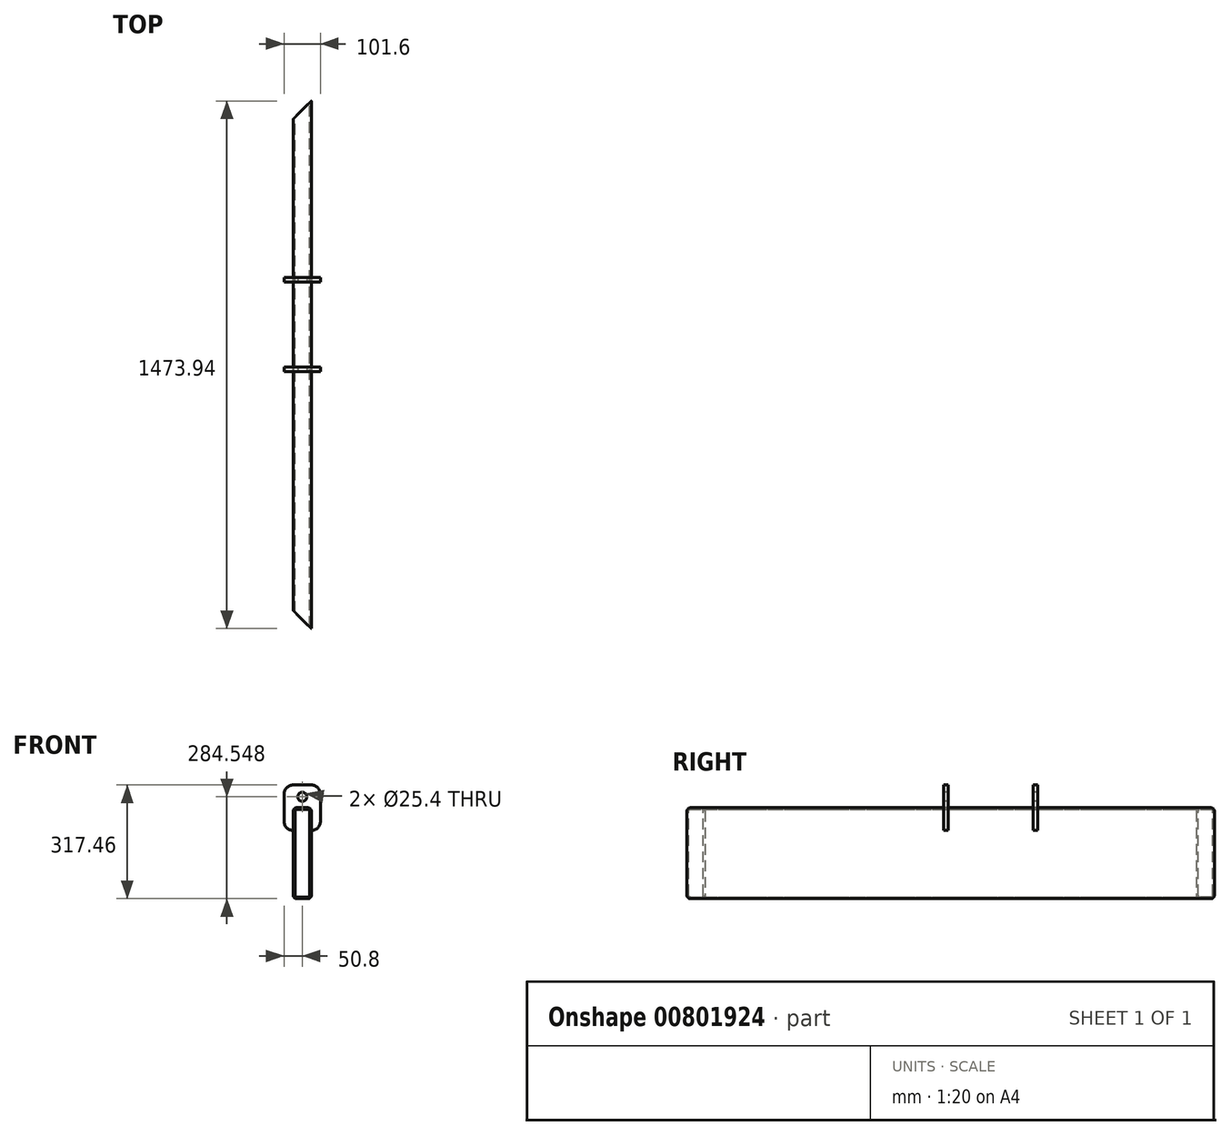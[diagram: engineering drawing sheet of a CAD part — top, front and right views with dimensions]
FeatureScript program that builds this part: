
annotation { "Feature Type Name" : "Feature", "Feature Type Description" : "" }
export const myFeature = defineFeature(function(context is Context, id is Id, definition is map)
    precondition{}
    {
        {
            var Q0;
            Q0=qCreatedBy(makeId("Front.planeOp"),FACE);
            var sketch = newSketch(context, id + "F0", { "sketchPlane" : qUnion([Q0])});
            skLineSegment(sketch, "E0.bottom", {"start": v(-9.52, 0) * mm, "end": v(-41.28, 0) * mm});
            skLineSegment(sketch, "E0.top", {"start": v(-9.53, 254) * mm, "end": v(-41.28, 254) * mm});
            skLineSegment(sketch, "E0.left", {"start": v(0, 9.53) * mm, "end": v(0, 244.47) * mm});
            skLineSegment(sketch, "E0.right", {"start": v(-50.8, 9.52) * mm, "end": v(-50.8, 244.47) * mm});
            skLineSegment(sketch, "E1.bottom", {"start": v(-41.3, 249.25) * mm, "end": v(-9.5, 249.25) * mm});
            skLineSegment(sketch, "E1.top", {"start": v(-41.3, 4.75) * mm, "end": v(-9.5, 4.75) * mm});
            skLineSegment(sketch, "E1.left", {"start": v(-46.05, 244.5) * mm, "end": v(-46.05, 9.5) * mm});
            skLineSegment(sketch, "E1.right", {"start": v(-4.75, 244.5) * mm, "end": v(-4.75, 9.5) * mm});
            skPoint(sketch, "E2.visualSharp", {"position": v(-46.05, 249.25) * mm});
            skArc(sketch, "E2.filletArc", {"start": v(-41.3, 249.25) * mm, "mid": v(-44.66, 247.86) * mm, "end": v(-46.05, 244.5) * mm});
            skPoint(sketch, "E3.visualSharp", {"position": v(-4.75, 249.25) * mm});
            skArc(sketch, "E3.filletArc", {"start": v(-4.75, 244.5) * mm, "mid": v(-6.14, 247.86) * mm, "end": v(-9.5, 249.25) * mm});
            skPoint(sketch, "E4.visualSharp", {"position": v(-4.75, 4.75) * mm});
            skArc(sketch, "E4.filletArc", {"start": v(-9.5, 4.75) * mm, "mid": v(-6.14, 6.14) * mm, "end": v(-4.75, 9.5) * mm});
            skPoint(sketch, "E5.visualSharp", {"position": v(-46.05, 4.75) * mm});
            skArc(sketch, "E5.filletArc", {"start": v(-46.05, 9.5) * mm, "mid": v(-44.66, 6.14) * mm, "end": v(-41.3, 4.75) * mm});
            skPoint(sketch, "E6.visualSharp", {"position": v(-50.8, 254) * mm});
            skArc(sketch, "E6.filletArc", {"start": v(-41.28, 254) * mm, "mid": v(-48.01, 251.21) * mm, "end": v(-50.8, 244.47) * mm});
            skPoint(sketch, "E7.visualSharp", {"position": v(0, 254) * mm});
            skArc(sketch, "E7.filletArc", {"start": v(0, 244.47) * mm, "mid": v(-2.79, 251.21) * mm, "end": v(-9.53, 254) * mm});
            skPoint(sketch, "E8.visualSharp", {"position": v(0, 0) * mm});
            skArc(sketch, "E8.filletArc", {"start": v(-9.52, 0) * mm, "mid": v(-2.79, 2.79) * mm, "end": v(0, 9.53) * mm});
            skPoint(sketch, "E9.visualSharp", {"position": v(-50.8, 0) * mm});
            skArc(sketch, "E9.filletArc", {"start": v(-50.8, 9.52) * mm, "mid": v(-48.01, 2.79) * mm, "end": v(-41.28, 0) * mm});
            skSolve(sketch);
        }
        {
            var Q0;
            Q0=qSketchRegion(id+"F0",true);
            extrude(context, id + "F1", {"entities" : qUnion([Q0]), "depth" : 1473.94 * mm});
        }
        {
            var Q0;
            Q0=makeQuery(id+"F1.opExtrude","SWEPT_FACE",FACE,{"disambiguationData":[OSD([sQuery(id+"F0.wireOp",EDGE,"E0.top")])]});
            var sketch = newSketch(context, id + "F2", { "sketchPlane" : qUnion([Q0])});
            skLineSegment(sketch, "E10", {"start": v(-50.8, -1473.94) * mm, "end": v(0, -1423.14) * mm});
            skLineSegment(sketch, "E11", {"start": v(0, -1423.14) * mm, "end": v(0, -1473.94) * mm});
            skLineSegment(sketch, "E12", {"start": v(0, -1473.94) * mm, "end": v(-50.8, -1473.94) * mm});
            skLineSegment(sketch, "E13", {"start": v(-50.8, 0) * mm, "end": v(0, -50.8) * mm});
            skLineSegment(sketch, "E14", {"start": v(0, -50.8) * mm, "end": v(0, 0) * mm});
            skLineSegment(sketch, "E15", {"start": v(0, 0) * mm, "end": v(-50.8, 0) * mm});
            skSolve(sketch);
        }
        {
            var Q0;
            Q0=qSketchRegion(id+"F2",true);
            extrude(context, id + "F3", {"entities" : qUnion([Q0]), "operationType" : NewBodyOperationType.REMOVE, "endBound" : BoundingType.THROUGH_ALL, "oppositeDirection" : true, "depth" : 25.4 * mm});
        }
        {
            var Q0;
            Q0=makeQuery(id+"F1.opExtrude","SWEPT_BODY",BODY,{"disambiguationData":[OSD([sQuery(id+"F0.wireOp",EDGE,"E0.bottom"),sQuery(id+"F0.wireOp",EDGE,"E0.top"),sQuery(id+"F0.wireOp",EDGE,"E0.left"),sQuery(id+"F0.wireOp",EDGE,"E0.right"),sQuery(id+"F0.wireOp",EDGE,"E1.bottom"),sQuery(id+"F0.wireOp",EDGE,"E1.top"),sQuery(id+"F0.wireOp",EDGE,"E1.left"),sQuery(id+"F0.wireOp",EDGE,"E1.right"),sQuery(id+"F0.wireOp",EDGE,"E2.filletArc"),sQuery(id+"F0.wireOp",EDGE,"E3.filletArc"),sQuery(id+"F0.wireOp",EDGE,"E4.filletArc"),sQuery(id+"F0.wireOp",EDGE,"E5.filletArc"),sQuery(id+"F0.wireOp",EDGE,"E6.filletArc"),sQuery(id+"F0.wireOp",EDGE,"E7.filletArc"),sQuery(id+"F0.wireOp",EDGE,"E8.filletArc"),sQuery(id+"F0.wireOp",EDGE,"E9.filletArc")])]});
            var Q1;
            Q1=makeQuery(id+"F1.opExtrude","SWEPT_EDGE",EDGE,{"disambiguationData":[OSD([sQuery(id+"F0.wireOp",EDGE,"E1.left"),sQuery(id+"F0.wireOp",EDGE,"E5.filletArc")])]});
            transform(context, id + "F4", {"entities" : qUnion([Q0]), "transformType" : TransformType.ROTATION, "transformAxis" : qUnion([Q1]), "angle" : 180 * degree, "makeCopy" : false});
        }
        {
            var Q0;
            Q0=qCreatedBy(makeId("Front.planeOp"),FACE);
            cPlane(context, id + "F5", {"entities" : qUnion([Q0]), "cplaneType" : CPlaneType.OFFSET, "offset" : 756.26 * mm, "width" : 150 * mm, "height" : 150 * mm});
        }
        {
            var Q0;
            Q0=qCreatedBy(id+"F5.planeOp",FACE);
            var sketch = newSketch(context, id + "F6", { "sketchPlane" : qUnion([Q0])});
            skCircle(sketch, "E16", {"center": v(0, 29.85) * mm, "radius": 12.7 * mm});
            skLineSegment(sketch, "E17", {"start": v(-25.4, 62.76) * mm, "end": v(25.4, 62.76) * mm});
            skLineSegment(sketch, "E18", {"start": v(50.8, 37.36) * mm, "end": v(50.8, -38.84) * mm});
            skLineSegment(sketch, "E19", {"start": v(-50.8, -38.84) * mm, "end": v(-50.8, 37.36) * mm});
            skPoint(sketch, "E20.visualSharp", {"position": v(-50.8, 62.76) * mm});
            skArc(sketch, "E20.filletArc", {"start": v(-25.4, 62.76) * mm, "mid": v(-43.36, 55.32) * mm, "end": v(-50.8, 37.36) * mm});
            skPoint(sketch, "E21.visualSharp", {"position": v(50.8, 62.76) * mm});
            skArc(sketch, "E21.filletArc", {"start": v(50.8, 37.36) * mm, "mid": v(43.36, 55.32) * mm, "end": v(25.4, 62.76) * mm});
            skPoint(sketch, "E22.visualSharp", {"position": v(50.8, -64.24) * mm});
            skArc(sketch, "E22.filletArc", {"start": v(25.4, -64.24) * mm, "mid": v(43.36, -56.8) * mm, "end": v(50.8, -38.84) * mm});
            skPoint(sketch, "E23.visualSharp", {"position": v(-50.8, -64.24) * mm});
            skArc(sketch, "E23.filletArc", {"start": v(-50.8, -38.84) * mm, "mid": v(-43.36, -56.8) * mm, "end": v(-25.4, -64.24) * mm});
            skLineSegment(sketch, "E24", {"start": v(-25.4, -64.24) * mm, "end": v(-25.4, -10.27) * mm});
            skLineSegment(sketch, "E25", {"start": v(-15.88, -0.74) * mm, "end": v(15.88, -0.74) * mm});
            skLineSegment(sketch, "E26", {"start": v(25.4, -10.27) * mm, "end": v(25.4, -64.24) * mm});
            skPoint(sketch, "E27.visualSharp", {"position": v(-25.4, -0.74) * mm});
            skArc(sketch, "E27.filletArc", {"start": v(-15.88, -0.74) * mm, "mid": v(-22.61, -3.53) * mm, "end": v(-25.4, -10.27) * mm});
            skPoint(sketch, "E28.visualSharp", {"position": v(25.4, -0.74) * mm});
            skArc(sketch, "E28.filletArc", {"start": v(25.4, -10.27) * mm, "mid": v(22.61, -3.53) * mm, "end": v(15.88, -0.74) * mm});
            skSolve(sketch);
        }
        {
            var Q0;
            Q0=qSketchRegion(id+"F6",true);
            extrude(context, id + "F7", {"entities" : qUnion([Q0]), "oppositeDirection" : true, "depth" : 12.7 * mm});
        }
        {
            var Q0;
            Q0=makeQuery(id+"F7.opExtrude","SWEPT_BODY",BODY,{"disambiguationData":[OSD([sQuery(id+"F6.wireOp",EDGE,"E16"),sQuery(id+"F6.wireOp",EDGE,"E17"),sQuery(id+"F6.wireOp",EDGE,"E18"),sQuery(id+"F6.wireOp",EDGE,"E19"),sQuery(id+"F6.wireOp",EDGE,"E20.filletArc"),sQuery(id+"F6.wireOp",EDGE,"E21.filletArc"),sQuery(id+"F6.wireOp",EDGE,"E22.filletArc"),sQuery(id+"F6.wireOp",EDGE,"E23.filletArc"),sQuery(id+"F6.wireOp",EDGE,"E24"),sQuery(id+"F6.wireOp",EDGE,"E25"),sQuery(id+"F6.wireOp",EDGE,"E26"),sQuery(id+"F6.wireOp",EDGE,"E27.filletArc"),sQuery(id+"F6.wireOp",EDGE,"E28.filletArc")])]});
            transform(context, id + "F8", {"entities" : qUnion([Q0]), "transformType" : TransformType.TRANSLATION_3D, "dx" : -66.7 * mm, "dy" : 0 * mm, "dz" : 19.7 * mm, "makeCopy" : false});
        }
        {
            var Q0;
            Q0=makeQuery(id+"F7.opExtrude","SWEPT_BODY",BODY,{"disambiguationData":[OSD([sQuery(id+"F6.wireOp",EDGE,"E16"),sQuery(id+"F6.wireOp",EDGE,"E17"),sQuery(id+"F6.wireOp",EDGE,"E18"),sQuery(id+"F6.wireOp",EDGE,"E19"),sQuery(id+"F6.wireOp",EDGE,"E20.filletArc"),sQuery(id+"F6.wireOp",EDGE,"E21.filletArc"),sQuery(id+"F6.wireOp",EDGE,"E22.filletArc"),sQuery(id+"F6.wireOp",EDGE,"E23.filletArc"),sQuery(id+"F6.wireOp",EDGE,"E24"),sQuery(id+"F6.wireOp",EDGE,"E25"),sQuery(id+"F6.wireOp",EDGE,"E26"),sQuery(id+"F6.wireOp",EDGE,"E27.filletArc"),sQuery(id+"F6.wireOp",EDGE,"E28.filletArc")])]});
            transform(context, id + "F9", {"entities" : qUnion([Q0]), "transformType" : TransformType.TRANSLATION_3D, "dx" : 0 * mm, "dy" : 250.16 * mm, "dz" : 0 * mm, "makeCopy" : true});
        }
    });
